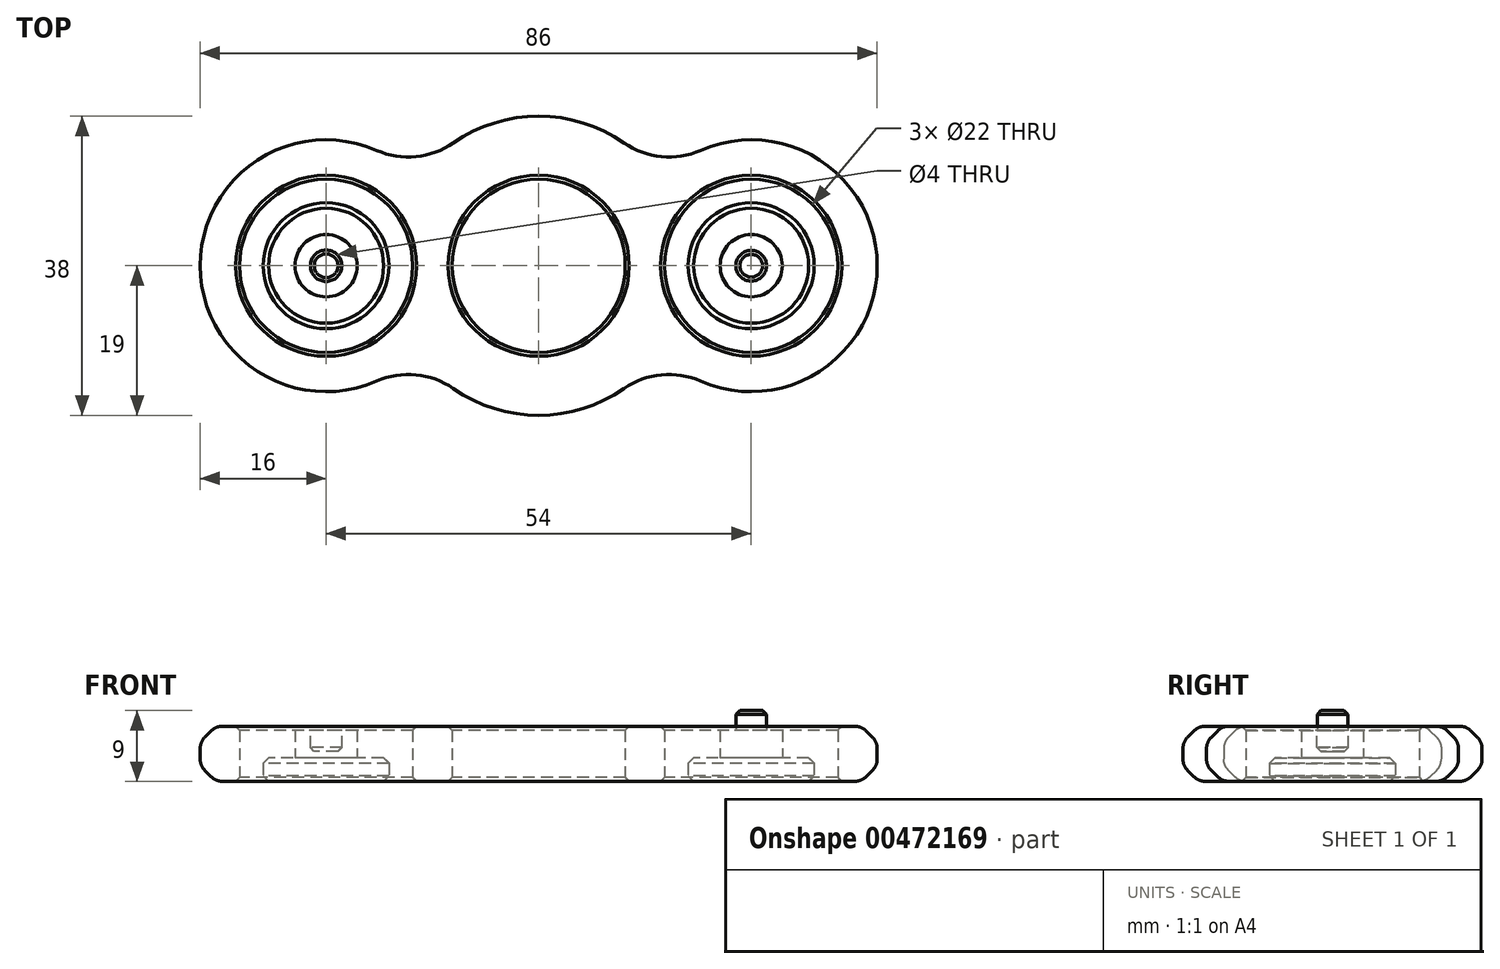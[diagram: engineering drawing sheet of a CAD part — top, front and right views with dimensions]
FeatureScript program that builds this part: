
annotation { "Feature Type Name" : "Feature", "Feature Type Description" : "" }
export const myFeature = defineFeature(function(context is Context, id is Id, definition is map)
    precondition{}
    {
        {
            var Q0;
            Q0=qCreatedBy(makeId("Top.planeOp"),FACE);
            var sketch = newSketch(context, id + "F0", { "sketchPlane" : qUnion([Q0])});
            skCircle(sketch, "E0", {"center": v(0, 0) * mm, "radius": 11 * mm});
            skCircle(sketch, "E1", {"center": v(-27, 0) * mm, "radius": 11 * mm});
            skCircle(sketch, "E2", {"center": v(27, 0) * mm, "radius": 11 * mm});
            skArc(sketch, "E3", {"start": v(-10.85, -15.6) * mm, "mid": v(0, -19) * mm, "end": v(10.85, -15.6) * mm});
            skArc(sketch, "E4", {"start": v(-20.57, 14.65) * mm, "mid": v(-43, 0) * mm, "end": v(-20.57, -14.65) * mm});
            skArc(sketch, "E5", {"start": v(20.57, -14.65) * mm, "mid": v(43, 0) * mm, "end": v(20.57, 14.65) * mm});
            skArc(sketch, "E6.trimOffspring", {"start": v(10.85, 15.6) * mm, "mid": v(0, 19) * mm, "end": v(-10.85, 15.6) * mm});
            skPoint(sketch, "E7.visualSharp", {"position": v(-15.44, 11.07) * mm});
            skArc(sketch, "E7.filletArc", {"start": v(-20.57, 14.65) * mm, "mid": v(-15.59, 13.86) * mm, "end": v(-10.85, 15.6) * mm});
            skPoint(sketch, "E8.visualSharp", {"position": v(-15.44, -11.07) * mm});
            skArc(sketch, "E8.filletArc", {"start": v(-10.85, -15.6) * mm, "mid": v(-15.59, -13.86) * mm, "end": v(-20.57, -14.65) * mm});
            skPoint(sketch, "E9.visualSharp", {"position": v(15.44, -11.07) * mm});
            skArc(sketch, "E9.filletArc", {"start": v(20.57, -14.65) * mm, "mid": v(15.59, -13.86) * mm, "end": v(10.85, -15.6) * mm});
            skPoint(sketch, "E10.visualSharp", {"position": v(15.44, 11.07) * mm});
            skArc(sketch, "E10.filletArc", {"start": v(10.85, 15.6) * mm, "mid": v(15.59, 13.86) * mm, "end": v(20.57, 14.65) * mm});
            skSolve(sketch);
        }
        {
            var Q0;
            Q0=makeQuery(id+"F0.imprint","IMPRINT",FACE,{"disambiguationData":[TD([[makeQuery(id+"F0.imprint","IMPRINT",EDGE,{"derivedFrom":sQuery(id+"F0.wireOp",EDGE,"E0")}),-1.0]])]});
            extrude(context, id + "F1", {"entities" : qUnion([Q0]), "depth" : 7 * mm});
        }
        {
            var Q0;
            Q0=makeQuery(id+"F1.opExtrude","CAP_EDGE",EDGE,{"disambiguationData":[OSD([sQuery(id+"F0.wireOp",EDGE,"E4")])],"isStart":false});
            var Q1;
            Q1=makeQuery(id+"F1.opExtrude","CAP_EDGE",EDGE,{"disambiguationData":[OSD([sQuery(id+"F0.wireOp",EDGE,"E4")])],"isStart":true});
            chamfer(context, id + "F2", {"entities" : qUnion([Q0, Q1]), "width" : 2 * mm, "tangentPropagation" : true});
        }
        {
            var Q0;
            Q0=makeQuery(id+"F1.opExtrude","CAP_EDGE",EDGE,{"disambiguationData":[OSD([sQuery(id+"F0.wireOp",EDGE,"E1")])],"isStart":false});
            var Q1;
            Q1=makeQuery(id+"F1.opExtrude","CAP_EDGE",EDGE,{"disambiguationData":[OSD([sQuery(id+"F0.wireOp",EDGE,"E1")])],"isStart":true});
            var Q2;
            Q2=makeQuery(id+"F1.opExtrude","CAP_EDGE",EDGE,{"disambiguationData":[OSD([sQuery(id+"F0.wireOp",EDGE,"E0")])],"isStart":false});
            var Q3;
            Q3=makeQuery(id+"F1.opExtrude","CAP_EDGE",EDGE,{"disambiguationData":[OSD([sQuery(id+"F0.wireOp",EDGE,"E0")])],"isStart":true});
            var Q4;
            Q4=makeQuery(id+"F1.opExtrude","CAP_EDGE",EDGE,{"disambiguationData":[OSD([sQuery(id+"F0.wireOp",EDGE,"E2")])],"isStart":false});
            var Q5;
            Q5=makeQuery(id+"F1.opExtrude","CAP_EDGE",EDGE,{"disambiguationData":[OSD([sQuery(id+"F0.wireOp",EDGE,"E2")])],"isStart":true});
            chamfer(context, id + "F3", {"entities" : qUnion([Q0, Q1, Q2, Q3, Q4, Q5]), "width" : 0.5 * mm, "tangentPropagation" : true});
        }
        {
            var Q0;
            {var subQ0=sQuery(id+"F0.wireOp",EDGE,"E4");Q0=makeQuery(id+"F2.opChamfer","BLEND_EDGE",EDGE,{"blendedFrom":[makeQuery(id+"F1.opExtrude","CAP_EDGE",EDGE,{"disambiguationData":[OSD([subQ0])],"isStart":false}),makeQuery(id+"F1.opExtrude","SWEPT_FACE",FACE,{"disambiguationData":[OSD([subQ0])]})],"blendedInto":[makeQuery(id+"F1.opExtrude","SWEPT_FACE",FACE,{"disambiguationData":[OSD([subQ0])]})]});}
            var Q1;
            {var subQ0=sQuery(id+"F0.wireOp",EDGE,"E4");Q1=makeQuery(id+"F2.opChamfer","BLEND_EDGE",EDGE,{"blendedFrom":[makeQuery(id+"F1.opExtrude","CAP_EDGE",EDGE,{"disambiguationData":[OSD([subQ0])],"isStart":true}),makeQuery(id+"F1.opExtrude","SWEPT_FACE",FACE,{"disambiguationData":[OSD([subQ0])]})],"blendedInto":[makeQuery(id+"F1.opExtrude","SWEPT_FACE",FACE,{"disambiguationData":[OSD([subQ0])]})]});}
            var Q2;
            {var subQ0=sQuery(id+"F0.wireOp",EDGE,"E4");Q2=makeQuery(id+"F2.opChamfer","BLEND_EDGE",EDGE,{"blendedFrom":[makeQuery(id+"F1.opExtrude","CAP_EDGE",EDGE,{"disambiguationData":[OSD([subQ0])],"isStart":false}),makeQuery(id+"F1.opExtrude","CAP_FACE",FACE,{"disambiguationData":[OSD([sQuery(id+"F0.wireOp",EDGE,"E0"),sQuery(id+"F0.wireOp",EDGE,"E1"),sQuery(id+"F0.wireOp",EDGE,"E2"),sQuery(id+"F0.wireOp",EDGE,"E3"),subQ0,sQuery(id+"F0.wireOp",EDGE,"E5"),sQuery(id+"F0.wireOp",EDGE,"E6.trimOffspring"),sQuery(id+"F0.wireOp",EDGE,"E7.filletArc"),sQuery(id+"F0.wireOp",EDGE,"E8.filletArc"),sQuery(id+"F0.wireOp",EDGE,"E9.filletArc"),sQuery(id+"F0.wireOp",EDGE,"E10.filletArc")])],"isStart":false})],"blendedInto":[makeQuery(id+"F1.opExtrude","CAP_FACE",FACE,{"disambiguationData":[OSD([sQuery(id+"F0.wireOp",EDGE,"E0"),sQuery(id+"F0.wireOp",EDGE,"E1"),sQuery(id+"F0.wireOp",EDGE,"E2"),sQuery(id+"F0.wireOp",EDGE,"E3"),subQ0,sQuery(id+"F0.wireOp",EDGE,"E5"),sQuery(id+"F0.wireOp",EDGE,"E6.trimOffspring"),sQuery(id+"F0.wireOp",EDGE,"E7.filletArc"),sQuery(id+"F0.wireOp",EDGE,"E8.filletArc"),sQuery(id+"F0.wireOp",EDGE,"E9.filletArc"),sQuery(id+"F0.wireOp",EDGE,"E10.filletArc")])],"isStart":false})]});}
            var Q3;
            {var subQ0=sQuery(id+"F0.wireOp",EDGE,"E4");Q3=makeQuery(id+"F2.opChamfer","BLEND_EDGE",EDGE,{"blendedFrom":[makeQuery(id+"F1.opExtrude","CAP_EDGE",EDGE,{"disambiguationData":[OSD([subQ0])],"isStart":true}),makeQuery(id+"F1.opExtrude","CAP_FACE",FACE,{"disambiguationData":[OSD([sQuery(id+"F0.wireOp",EDGE,"E0"),sQuery(id+"F0.wireOp",EDGE,"E1"),sQuery(id+"F0.wireOp",EDGE,"E2"),sQuery(id+"F0.wireOp",EDGE,"E3"),subQ0,sQuery(id+"F0.wireOp",EDGE,"E5"),sQuery(id+"F0.wireOp",EDGE,"E6.trimOffspring"),sQuery(id+"F0.wireOp",EDGE,"E7.filletArc"),sQuery(id+"F0.wireOp",EDGE,"E8.filletArc"),sQuery(id+"F0.wireOp",EDGE,"E9.filletArc"),sQuery(id+"F0.wireOp",EDGE,"E10.filletArc")])],"isStart":true})],"blendedInto":[makeQuery(id+"F1.opExtrude","CAP_FACE",FACE,{"disambiguationData":[OSD([sQuery(id+"F0.wireOp",EDGE,"E0"),sQuery(id+"F0.wireOp",EDGE,"E1"),sQuery(id+"F0.wireOp",EDGE,"E2"),sQuery(id+"F0.wireOp",EDGE,"E3"),subQ0,sQuery(id+"F0.wireOp",EDGE,"E5"),sQuery(id+"F0.wireOp",EDGE,"E6.trimOffspring"),sQuery(id+"F0.wireOp",EDGE,"E7.filletArc"),sQuery(id+"F0.wireOp",EDGE,"E8.filletArc"),sQuery(id+"F0.wireOp",EDGE,"E9.filletArc"),sQuery(id+"F0.wireOp",EDGE,"E10.filletArc")])],"isStart":true})]});}
            fillet(context, id + "F4", {"entities" : qUnion([Q0, Q1, Q2, Q3]), "radius" : 2 * mm, "tangentPropagation" : true, "allowEdgeOverflow" : false});
        }
        {
            var Q0;
            Q0=qCreatedBy(makeId("Top.planeOp"),FACE);
            var sketch = newSketch(context, id + "F5", { "sketchPlane" : qUnion([Q0])});
            skCircle(sketch, "E11", {"center": v(-27, 0) * mm, "radius": 8 * mm});
            skCircle(sketch, "E12", {"center": v(27, 0) * mm, "radius": 8 * mm});
            skSolve(sketch);
        }
        {
            var Q0;
            Q0=makeQuery(id+"F5.imprint","IMPRINT",FACE,{"disambiguationData":[TD([[makeQuery(id+"F5.imprint","IMPRINT",EDGE,{"derivedFrom":sQuery(id+"F5.wireOp",EDGE,"E11")}),1.0]])]});
            var Q1;
            Q1=makeQuery(id+"F5.imprint","IMPRINT",FACE,{"disambiguationData":[TD([[makeQuery(id+"F5.imprint","IMPRINT",EDGE,{"derivedFrom":sQuery(id+"F5.wireOp",EDGE,"E12")}),1.0]])]});
            extrude(context, id + "F6", {"entities" : qUnion([Q0, Q1]), "depth" : 3 * mm});
        }
        {
            var Q0;
            Q0=makeQuery(id+"F6.opExtrude","CAP_EDGE",EDGE,{"disambiguationData":[OSD([sQuery(id+"F5.wireOp",EDGE,"E11")])],"isStart":true});
            var Q1;
            Q1=makeQuery(id+"F6.opExtrude","CAP_EDGE",EDGE,{"disambiguationData":[OSD([sQuery(id+"F5.wireOp",EDGE,"E12")])],"isStart":true});
            var Q2;
            Q2=makeQuery(id+"F6.opExtrude","CAP_EDGE",EDGE,{"disambiguationData":[OSD([sQuery(id+"F5.wireOp",EDGE,"E11")])],"isStart":false});
            var Q3;
            Q3=makeQuery(id+"F6.opExtrude","CAP_EDGE",EDGE,{"disambiguationData":[OSD([sQuery(id+"F5.wireOp",EDGE,"E12")])],"isStart":false});
            chamfer(context, id + "F7", {"entities" : qUnion([Q0, Q1, Q2, Q3]), "width" : 0.7 * mm, "tangentPropagation" : true});
        }
        {
            var Q0;
            Q0=makeQuery(id+"F6.opExtrude","CAP_FACE",FACE,{"disambiguationData":[OSD([sQuery(id+"F5.wireOp",EDGE,"E12")])],"isStart":false});
            var sketch = newSketch(context, id + "F8", { "sketchPlane" : qUnion([Q0])});
            skCircle(sketch, "E13", {"center": v(27, 0) * mm, "radius": 3.95 * mm});
            skSolve(sketch);
        }
        {
            var Q0;
            Q0 = qSketchRegion(id + "F8", true);
            extrude(context, id + "F9", {"entities" : qUnion([Q0]), "operationType" : NewBodyOperationType.ADD, "depth" : 3.5 * mm});
        }
        {
            var Q0;
            Q0=makeQuery(id+"F6.opExtrude","CAP_FACE",FACE,{"disambiguationData":[OSD([sQuery(id+"F5.wireOp",EDGE,"E11")])],"isStart":false});
            var sketch = newSketch(context, id + "F10", { "sketchPlane" : qUnion([Q0])});
            skCircle(sketch, "E14", {"center": v(-27, 0) * mm, "radius": 3.95 * mm});
            skSolve(sketch);
        }
        {
            var Q0;
            Q0 = qSketchRegion(id + "F10", true);
            extrude(context, id + "F11", {"entities" : qUnion([Q0]), "operationType" : NewBodyOperationType.ADD, "depth" : 3.5 * mm});
        }
        {
            var Q0;
            Q0=makeQuery(id+"F9.opExtrude","CAP_FACE",FACE,{"disambiguationData":[OSD([sQuery(id+"F8.wireOp",EDGE,"E13")])],"isStart":false});
            var sketch = newSketch(context, id + "F12", { "sketchPlane" : qUnion([Q0])});
            skCircle(sketch, "E15", {"center": v(27, 0) * mm, "radius": 1.95 * mm});
            skSolve(sketch);
        }
        {
            var Q0;
            Q0=makeQuery(id+"F11.opExtrude","CAP_FACE",FACE,{"disambiguationData":[OSD([sQuery(id+"F10.wireOp",EDGE,"E14")])],"isStart":false});
            var sketch = newSketch(context, id + "F13", { "sketchPlane" : qUnion([Q0])});
            skCircle(sketch, "E16", {"center": v(-27, 0) * mm, "radius": 2 * mm});
            skSolve(sketch);
        }
        {
            var Q0;
            Q0=makeQuery(id+"F13.imprint","IMPRINT",FACE,{"disambiguationData":[TD([[makeQuery(id+"F13.imprint","IMPRINT",EDGE,{"derivedFrom":sQuery(id+"F13.wireOp",EDGE,"E16")}),1.0]])]});
            extrude(context, id + "F14", {"entities" : qUnion([Q0]), "operationType" : NewBodyOperationType.REMOVE, "oppositeDirection" : true, "depth" : 2.7 * mm});
        }
        {
            var Q0;
            Q0=makeQuery(id+"F12.imprint","IMPRINT",FACE,{"disambiguationData":[TD([[makeQuery(id+"F12.imprint","IMPRINT",EDGE,{"derivedFrom":sQuery(id+"F12.wireOp",EDGE,"E15")}),1.0]])]});
            extrude(context, id + "F15", {"entities" : qUnion([Q0]), "operationType" : NewBodyOperationType.ADD, "depth" : 2.5 * mm});
        }
        {
            var Q0;
            Q0=makeQuery(id+"F15.opExtrude","CAP_EDGE",EDGE,{"disambiguationData":[OSD([sQuery(id+"F12.wireOp",EDGE,"E15")])],"isStart":false});
            var Q1;
            Q1=makeQuery(id+"F15.opExtrude","CAP_EDGE",EDGE,{"disambiguationData":[OSD([sQuery(id+"F12.wireOp",EDGE,"E15")])],"isStart":true});
            var Q2;
            Q2=makeQuery(id+"F14.boolean.opBoolean","COPY",EDGE,{"derivedFrom":makeQuery(id+"F14.opExtrude","CAP_EDGE",EDGE,{"disambiguationData":[OSD([sQuery(id+"F13.wireOp",EDGE,"E16")])],"isStart":true})});
            var Q3;
            Q3=makeQuery(id+"F14.boolean.opBoolean","COPY",EDGE,{"derivedFrom":makeQuery(id+"F14.opExtrude","CAP_EDGE",EDGE,{"disambiguationData":[OSD([sQuery(id+"F13.wireOp",EDGE,"E16")])],"isStart":false})});
            var Q4;
            Q4=makeQuery(id+"F11.opExtrude","CAP_EDGE",EDGE,{"disambiguationData":[OSD([sQuery(id+"F10.wireOp",EDGE,"E14")])],"isStart":true});
            var Q5;
            Q5=makeQuery(id+"F9.opExtrude","CAP_EDGE",EDGE,{"disambiguationData":[OSD([sQuery(id+"F8.wireOp",EDGE,"E13")])],"isStart":true});
            chamfer(context, id + "F16", {"entities" : qUnion([Q0, Q1, Q2, Q3, Q4, Q5]), "width" : 0.5 * mm, "tangentPropagation" : true});
        }
    });
